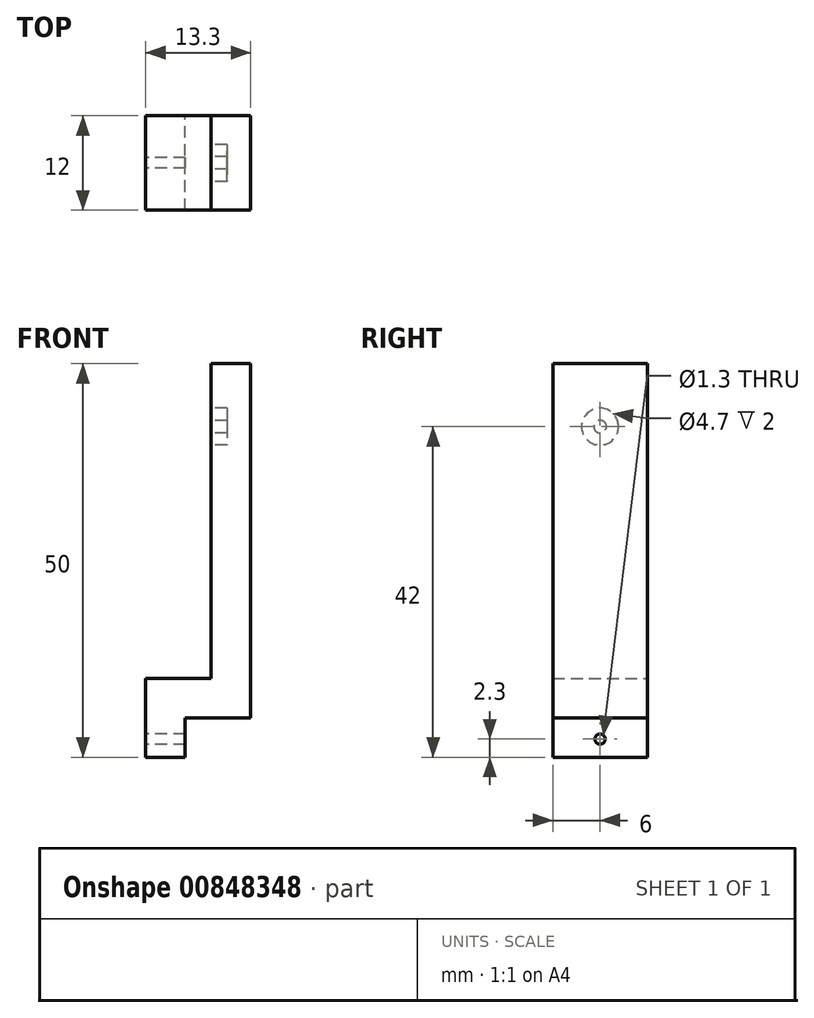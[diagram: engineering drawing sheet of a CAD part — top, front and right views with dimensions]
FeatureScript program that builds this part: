
annotation { "Feature Type Name" : "Feature", "Feature Type Description" : "" }
export const myFeature = defineFeature(function(context is Context, id is Id, definition is map)
    precondition{}
    {
        {
            var Q0;
            Q0=qCreatedBy(makeId("Front.planeOp"),FACE);
            var sketch = newSketch(context, id + "F0", { "sketchPlane" : qUnion([Q0])});
            skLineSegment(sketch, "E0", {"start": v(-13.3, -5) * mm, "end": v(-8.3, -5) * mm});
            skLineSegment(sketch, "E1", {"start": v(-8.3, -5) * mm, "end": v(-8.3, 0) * mm});
            skLineSegment(sketch, "E2", {"start": v(-8.3, 0) * mm, "end": v(0, 0) * mm});
            skLineSegment(sketch, "E3", {"start": v(0, 0) * mm, "end": v(0, 45) * mm});
            skLineSegment(sketch, "E4", {"start": v(0, 45) * mm, "end": v(-5, 45) * mm});
            skLineSegment(sketch, "E5", {"start": v(-5, 45) * mm, "end": v(-5, 5) * mm});
            skLineSegment(sketch, "E6", {"start": v(-5, 5) * mm, "end": v(-13.3, 5) * mm});
            skLineSegment(sketch, "E7", {"start": v(-13.3, 5) * mm, "end": v(-13.3, -5) * mm});
            skSolve(sketch);
        }
        {
            var Q0;
            Q0=makeQuery(id+"F0.imprint","IMPRINT",FACE,{"disambiguationData":[TD([[makeQuery(id+"F0.imprint","IMPRINT",EDGE,{"derivedFrom":sQuery(id+"F0.wireOp",EDGE,"E0")}),1.0]])]});
            extrude(context, id + "F1", {"entities" : qUnion([Q0]), "depth" : 12 * mm, "offsetDistance" : 25 * mm});
        }
        {
            var Q0;
            Q0=makeQuery(id+"F1.opExtrude","SWEPT_FACE",FACE,{"disambiguationData":[OSD([sQuery(id+"F0.wireOp",EDGE,"E7")])]});
            var sketch = newSketch(context, id + "F2", { "sketchPlane" : qUnion([Q0])});
            skCircle(sketch, "E8", {"center": v(6, -2.7) * mm, "radius": 0.65 * mm});
            skSolve(sketch);
        }
        {
            var Q0;
            Q0=makeQuery(id+"F2.imprint","IMPRINT",FACE,{"disambiguationData":[TD([[makeQuery(id+"F2.imprint","IMPRINT",EDGE,{"derivedFrom":sQuery(id+"F2.wireOp",EDGE,"E8")}),1.0]])]});
            extrude(context, id + "F3", {"entities" : qUnion([Q0]), "operationType" : NewBodyOperationType.REMOVE, "oppositeDirection" : true, "depth" : 5 * mm, "offsetDistance" : 25 * mm});
        }
        {
            var Q0;
            Q0=makeQuery(id+"F1.opExtrude","SWEPT_FACE",FACE,{"disambiguationData":[OSD([sQuery(id+"F0.wireOp",EDGE,"E5")])]});
            var sketch = newSketch(context, id + "F4", { "sketchPlane" : qUnion([Q0])});
            skCircle(sketch, "E9", {"center": v(6, 37) * mm, "radius": 2.35 * mm});
            skCircle(sketch, "E10", {"center": v(6, 37) * mm, "radius": 0.8 * mm});
            skSolve(sketch);
        }
        {
            var Q0;
            Q0=makeQuery(id+"F4.imprint","IMPRINT",FACE,{"disambiguationData":[TD([[makeQuery(id+"F4.imprint","IMPRINT",EDGE,{"derivedFrom":sQuery(id+"F4.wireOp",EDGE,"E9")}),1.0]])]});
            extrude(context, id + "F5", {"entities" : qUnion([Q0]), "operationType" : NewBodyOperationType.REMOVE, "oppositeDirection" : true, "depth" : 2 * mm, "offsetDistance" : 25 * mm});
        }
    });
